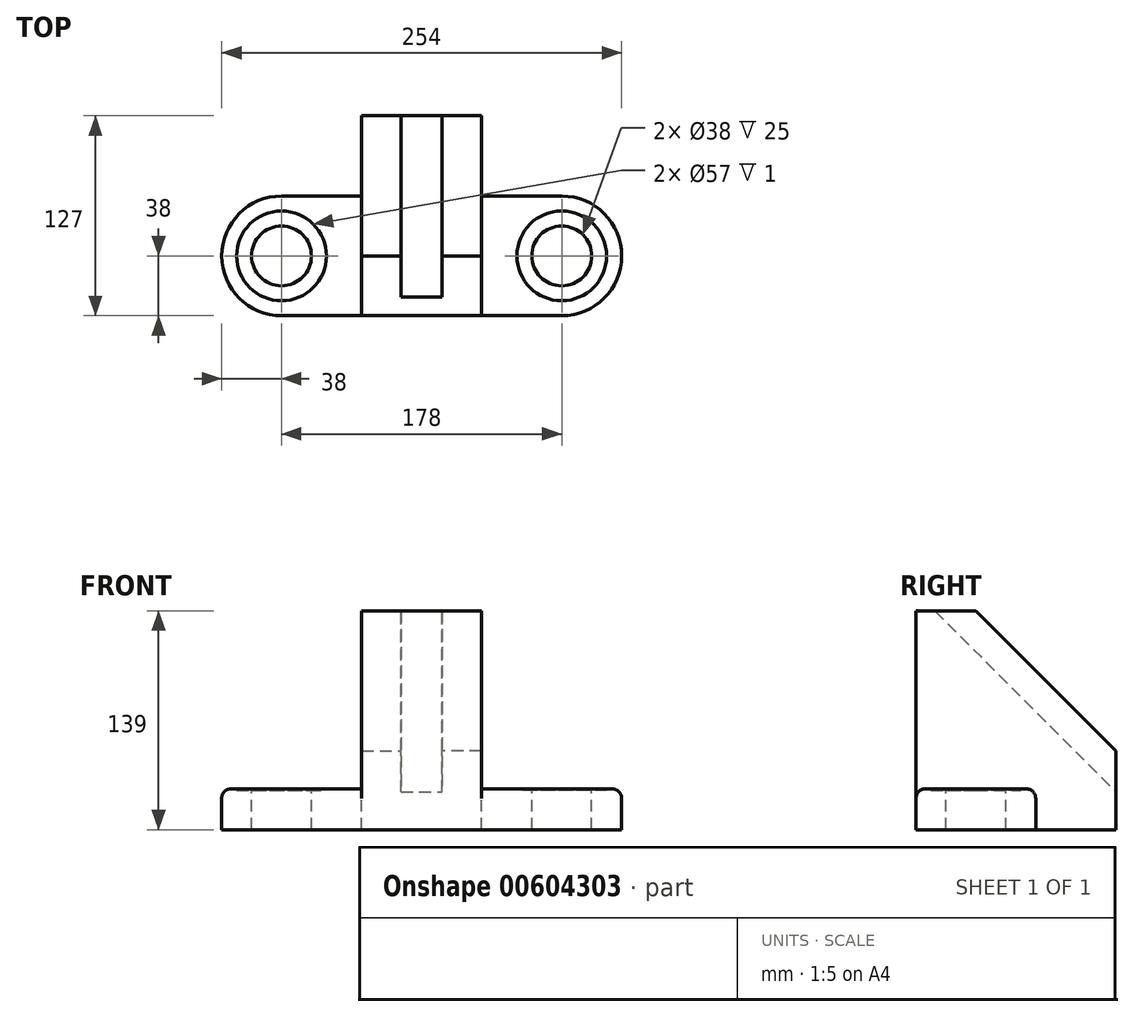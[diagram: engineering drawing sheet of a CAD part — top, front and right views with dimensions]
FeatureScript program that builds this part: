
annotation { "Feature Type Name" : "Feature", "Feature Type Description" : "" }
export const myFeature = defineFeature(function(context is Context, id is Id, definition is map)
    precondition{}
    {
        {
            var Q0;
            Q0=qCreatedBy(makeId("Right.planeOp"),FACE);
            var sketch = newSketch(context, id + "F0", { "sketchPlane" : qUnion([Q0])});
            skLineSegment(sketch, "E0", {"start": v(0, 0) * mm, "end": v(-127, 0) * mm});
            skLineSegment(sketch, "E1", {"start": v(-127, 0) * mm, "end": v(-127, 139) * mm});
            skLineSegment(sketch, "E2", {"start": v(-127, 139) * mm, "end": v(-89, 139) * mm});
            skLineSegment(sketch, "E3", {"start": v(0, 0) * mm, "end": v(0, 50) * mm});
            skLineSegment(sketch, "E4", {"start": v(0, 50) * mm, "end": v(-89, 139) * mm});
            skSolve(sketch);
        }
        {
            var Q0;
            Q0=makeQuery(id+"F0.imprint","IMPRINT",FACE,{"disambiguationData":[TD([[makeQuery(id+"F0.imprint","IMPRINT",EDGE,{"derivedFrom":sQuery(id+"F0.wireOp",EDGE,"E0")}),-1.0]])]});
            extrude(context, id + "F1", {"entities" : qUnion([Q0]), "depth" : 25 * mm, "offsetDistance" : 25 * mm});
        }
        {
            var Q0;
            Q0=makeQuery(id+"F1.opExtrude","CAP_FACE",FACE,{"disambiguationData":[OSD([sQuery(id+"F0.wireOp",EDGE,"E0"),sQuery(id+"F0.wireOp",EDGE,"E1"),sQuery(id+"F0.wireOp",EDGE,"E2"),sQuery(id+"F0.wireOp",EDGE,"E3"),sQuery(id+"F0.wireOp",EDGE,"E4")])],"isStart":true});
            var sketch = newSketch(context, id + "F2", { "sketchPlane" : qUnion([Q0])});
            skLineSegment(sketch, "E5", {"start": v(0, 0) * mm, "end": v(127, 0) * mm});
            skLineSegment(sketch, "E6", {"start": v(127, 0) * mm, "end": v(127, 139) * mm});
            skLineSegment(sketch, "E7", {"start": v(127, 139) * mm, "end": v(115, 139) * mm});
            skLineSegment(sketch, "E8", {"start": v(115, 139) * mm, "end": v(0, 24) * mm});
            skLineSegment(sketch, "E9", {"start": v(0, 24) * mm, "end": v(0, 0) * mm});
            skSolve(sketch);
        }
        {
            var Q0;
            Q0=makeQuery(id+"F2.imprint","IMPRINT",FACE,{"disambiguationData":[TD([[makeQuery(id+"F2.imprint","IMPRINT",EDGE,{"derivedFrom":sQuery(id+"F2.wireOp",EDGE,"E5")}),1.0]])]});
            extrude(context, id + "F3", {"entities" : qUnion([Q0]), "operationType" : NewBodyOperationType.ADD, "depth" : 13 * mm, "offsetDistance" : 25 * mm});
        }
        {
            var Q0;
            Q0=makeQuery(id+"F1.opExtrude","CAP_FACE",FACE,{"disambiguationData":[OSD([sQuery(id+"F0.wireOp",EDGE,"E0"),sQuery(id+"F0.wireOp",EDGE,"E1"),sQuery(id+"F0.wireOp",EDGE,"E2"),sQuery(id+"F0.wireOp",EDGE,"E3"),sQuery(id+"F0.wireOp",EDGE,"E4")])],"isStart":false});
            var sketch = newSketch(context, id + "F4", { "sketchPlane" : qUnion([Q0])});
            skLineSegment(sketch, "E10", {"start": v(-127, 0) * mm, "end": v(-51, 0) * mm});
            skLineSegment(sketch, "E11", {"start": v(-51, 0) * mm, "end": v(-51, 26) * mm});
            skLineSegment(sketch, "E12", {"start": v(-51, 26) * mm, "end": v(-127, 26) * mm});
            skLineSegment(sketch, "E13", {"start": v(-127, 26) * mm, "end": v(-127, 0) * mm});
            skSolve(sketch);
        }
        {
            var Q0;
            Q0=makeQuery(id+"F4.imprint","IMPRINT",FACE,{"disambiguationData":[TD([[makeQuery(id+"F4.imprint","IMPRINT",EDGE,{"derivedFrom":sQuery(id+"F4.wireOp",EDGE,"E10")}),-1.0]])]});
            extrude(context, id + "F5", {"entities" : qUnion([Q0]), "operationType" : NewBodyOperationType.ADD, "depth" : 89 * mm, "offsetDistance" : 25 * mm});
        }
        {
            var Q0;
            Q0=makeQuery(id+"F5.opExtrude","SWEPT_FACE",FACE,{"disambiguationData":[OSD([sQuery(id+"F4.wireOp",EDGE,"E12")])]});
            var sketch = newSketch(context, id + "F6", { "sketchPlane" : qUnion([Q0])});
            skCircle(sketch, "E14", {"center": v(76, -89) * mm, "radius": 38 * mm});
            skSolve(sketch);
        }
        {
            var Q0;
            {var subQ0=sQuery(id+"F6.wireOp",EDGE,"E14");var subQ1=sQuery(id+"F4.wireOp",EDGE,"E12");var subQ4=makeQuery(id+"F5.opExtrude","CAP_EDGE",EDGE,{"disambiguationData":[OSD([subQ1])],"isStart":false});var subQ5=makeQuery(id+"F6.imprint","INTERSECT",VERTEX,{"derivedFrom":[subQ4,subQ0]});Q0=makeQuery(id+"F6.imprint","IMPRINT",FACE,{"disambiguationData":[TD([[makeQuery(id+"F6.imprint","IMPRINT",EDGE,{"disambiguationData":[TD([[subQ5,-1.0]])],"derivedFrom":subQ0}),-1.0]])]});}
            var Q1;
            {var subQ0=sQuery(id+"F6.wireOp",EDGE,"E14");var subQ1=sQuery(id+"F4.wireOp",EDGE,"E12");var subQ2=makeQuery(id+"F5.opExtrude","CAP_EDGE",EDGE,{"disambiguationData":[OSD([subQ1])],"isStart":false});var subQ3=makeQuery(id+"F6.imprint","INTERSECT",VERTEX,{"derivedFrom":[subQ2,subQ0]});Q1=makeQuery(id+"F6.imprint","IMPRINT",FACE,{"disambiguationData":[TD([[makeQuery(id+"F6.imprint","IMPRINT",EDGE,{"disambiguationData":[TD([[subQ3,1.0]])],"derivedFrom":subQ0}),-1.0]])]});}
            extrude(context, id + "F7", {"entities" : qUnion([Q0, Q1]), "operationType" : NewBodyOperationType.REMOVE, "endBound" : BoundingType.THROUGH_ALL, "oppositeDirection" : true, "depth" : 25 * mm, "offsetDistance" : 25 * mm});
        }
        {
            var Q0;
            Q0=qCreatedBy(makeId("Right.planeOp"),FACE);
            cPlane(context, id + "F8", {"entities" : qUnion([Q0]), "cplaneType" : CPlaneType.OFFSET, "offset" : 13 * mm, "oppositeDirection" : true, "width" : 150 * mm, "height" : 150 * mm});
        }
        {
            var Q0;
            Q0=makeQuery(id+"F5.opExtrude","SWEPT_FACE",FACE,{"disambiguationData":[OSD([sQuery(id+"F4.wireOp",EDGE,"E12")])]});
            var sketch = newSketch(context, id + "F9", { "sketchPlane" : qUnion([Q0])});
            skCircle(sketch, "E15", {"center": v(76, -89) * mm, "radius": 28.5 * mm});
            skCircle(sketch, "E16", {"center": v(76, -89) * mm, "radius": 19 * mm});
            skSolve(sketch);
        }
        {
            var Q0;
            Q0=makeQuery(id+"F9.imprint","IMPRINT",FACE,{"disambiguationData":[TD([[makeQuery(id+"F9.imprint","IMPRINT",EDGE,{"derivedFrom":sQuery(id+"F9.wireOp",EDGE,"E16")}),1.0]])]});
            extrude(context, id + "F10", {"entities" : qUnion([Q0]), "operationType" : NewBodyOperationType.REMOVE, "endBound" : BoundingType.THROUGH_ALL, "oppositeDirection" : true, "depth" : 25 * mm, "offsetDistance" : 25 * mm});
        }
        {
            var Q0;
            Q0=makeQuery(id+"F9.imprint","IMPRINT",FACE,{"disambiguationData":[TD([[makeQuery(id+"F9.imprint","IMPRINT",EDGE,{"derivedFrom":sQuery(id+"F9.wireOp",EDGE,"E15")}),1.0]])]});
            extrude(context, id + "F11", {"entities" : qUnion([Q0]), "operationType" : NewBodyOperationType.REMOVE, "oppositeDirection" : true, "depth" : 1 * mm, "offsetDistance" : 25 * mm});
        }
        {
            var Q0;
            Q0=makeQuery(id+"F5.opExtrude","SWEPT_EDGE",EDGE,{"disambiguationData":[OSD([sQuery(id+"F4.wireOp",EDGE,"E11"),sQuery(id+"F4.wireOp",EDGE,"E12")])]});
            var Q1;
            {var subQ0=sQuery(id+"F6.wireOp",EDGE,"E14");var subQ1=sQuery(id+"F4.wireOp",EDGE,"E12");var subQ2=makeQuery(id+"F6.imprint","INTERSECT",VERTEX,{"derivedFrom":[makeQuery(id+"F5.opExtrude","CAP_EDGE",EDGE,{"disambiguationData":[OSD([subQ1])],"isStart":false}),subQ0]});Q1=makeQuery(id+"F7.boolean.opBoolean","TWEAK_EDGE",EDGE,{"derivedFrom":[makeQuery(id+"F7.opExtrude","CAP_EDGE",EDGE,{"disambiguationData":[OSD([subQ0]),TDD([makeQuery(id+"F6.imprint","IMPRINT",EDGE,{"disambiguationData":[TD([[subQ2,-1.0]])],"derivedFrom":subQ0})])],"isStart":true}),makeQuery(id+"F7.opExtrude","CAP_EDGE",EDGE,{"disambiguationData":[OSD([subQ0]),TDD([makeQuery(id+"F6.imprint","IMPRINT",EDGE,{"disambiguationData":[TD([[subQ2,1.0]])],"derivedFrom":subQ0})])],"isStart":true})]});}
            var Q2;
            Q2=makeQuery(id+"F5.opExtrude","SWEPT_EDGE",EDGE,{"disambiguationData":[OSD([sQuery(id+"F0.wireOp",EDGE,"E1"),sQuery(id+"F4.wireOp",EDGE,"E12"),sQuery(id+"F4.wireOp",EDGE,"E13")])]});
            fillet(context, id + "F12", {"entities" : qUnion([Q0, Q1, Q2]), "radius" : 6 * mm, "tangentPropagation" : true, "allowEdgeOverflow" : false});
        }
        {
            var Q0;
            Q0=makeQuery(id+"F1.opExtrude","SWEPT_BODY",BODY,{"disambiguationData":[OSD([sQuery(id+"F0.wireOp",EDGE,"E0"),sQuery(id+"F0.wireOp",EDGE,"E1"),sQuery(id+"F0.wireOp",EDGE,"E2"),sQuery(id+"F0.wireOp",EDGE,"E3"),sQuery(id+"F0.wireOp",EDGE,"E4")])]});
            var Q1;
            Q1=qCreatedBy(id+"F8.planeOp",FACE);
            mirror(context, id + "F13", {"operationType" : NewBodyOperationType.ADD, "entities" : qUnion([Q0]), "mirrorPlane" : qUnion([Q1])});
        }
    });
